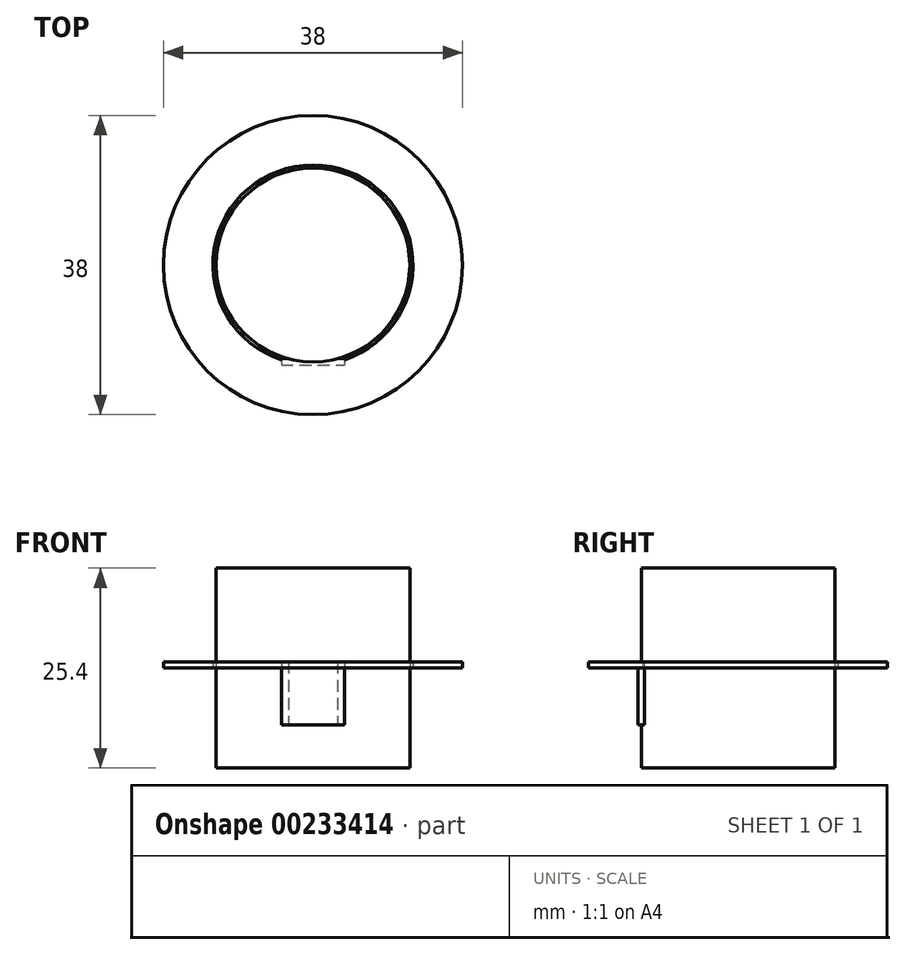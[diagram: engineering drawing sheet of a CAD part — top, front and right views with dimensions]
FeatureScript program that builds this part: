
annotation { "Feature Type Name" : "Feature", "Feature Type Description" : "" }
export const myFeature = defineFeature(function(context is Context, id is Id, definition is map)
    precondition{}
    {
        {
            var Q0;
            Q0=qCreatedBy(makeId("Top.planeOp"),FACE);
            var sketch = newSketch(context, id + "F0", { "sketchPlane" : qUnion([Q0])});
            skCircle(sketch, "E0", {"center": v(0, 0) * mm, "radius": 19 * mm});
            skCircle(sketch, "E1", {"center": v(0, 0) * mm, "radius": 12.7 * mm});
            skSolve(sketch);
        }
        {
            var Q0;
            Q0=makeQuery(id+"F0.imprint","IMPRINT",FACE,{"disambiguationData":[TD([[makeQuery(id+"F0.imprint","IMPRINT",EDGE,{"derivedFrom":sQuery(id+"F0.wireOp",EDGE,"E0")}),1.0]])]});
            extrude(context, id + "F1", {"entities" : qUnion([Q0]), "depth" : 0.8 * mm});
        }
        {
            var Q0;
            Q0=makeQuery(id+"F1.opExtrude","CAP_FACE",FACE,{"disambiguationData":[OSD([sQuery(id+"F0.wireOp",EDGE,"E0"),sQuery(id+"F0.wireOp",EDGE,"E1")])],"isStart":false});
            var sketch = newSketch(context, id + "F2", { "sketchPlane" : qUnion([Q0])});
            skLineSegment(sketch, "E2.bottom", {"start": v(-4, -11.9) * mm, "end": v(4, -11.9) * mm});
            skLineSegment(sketch, "E2.top", {"start": v(-4, -12.7) * mm, "end": v(4, -12.7) * mm});
            skLineSegment(sketch, "E2.left", {"start": v(-4, -11.9) * mm, "end": v(-4, -12.7) * mm});
            skLineSegment(sketch, "E2.right", {"start": v(4, -11.9) * mm, "end": v(4, -12.7) * mm});
            skLineSegment(sketch, "E3", {"start": v(0, 0) * mm, "end": v(0, -19) * mm, "construction": true});
            skPoint(sketch, "E4", {"position": v(0, -11.9) * mm});
            skPoint(sketch, "E5", {"position": v(0, -12.7) * mm});
            skSolve(sketch);
        }
        {
            var Q0;
            Q0 = qSketchRegion(id + "F2", true);
            extrude(context, id + "F3", {"entities" : qUnion([Q0]), "operationType" : NewBodyOperationType.ADD, "oppositeDirection" : true, "depth" : 8 * mm});
        }
        {
            var Q0;
            Q0=qCreatedBy(makeId("Top.planeOp"),FACE);
            var sketch = newSketch(context, id + "F4", { "sketchPlane" : qUnion([Q0])});
            skCircle(sketch, "E6", {"center": v(0, 0) * mm, "radius": 12.3 * mm});
            skSolve(sketch);
        }
        {
            var Q0;
            Q0 = qSketchRegion(id + "F4", true);
            extrude(context, id + "F5", {"entities" : qUnion([Q0]), "operationType" : NewBodyOperationType.ADD, "endBound" : BoundingType.SYMMETRIC, "depth" : 25.4 * mm});
        }
    });
